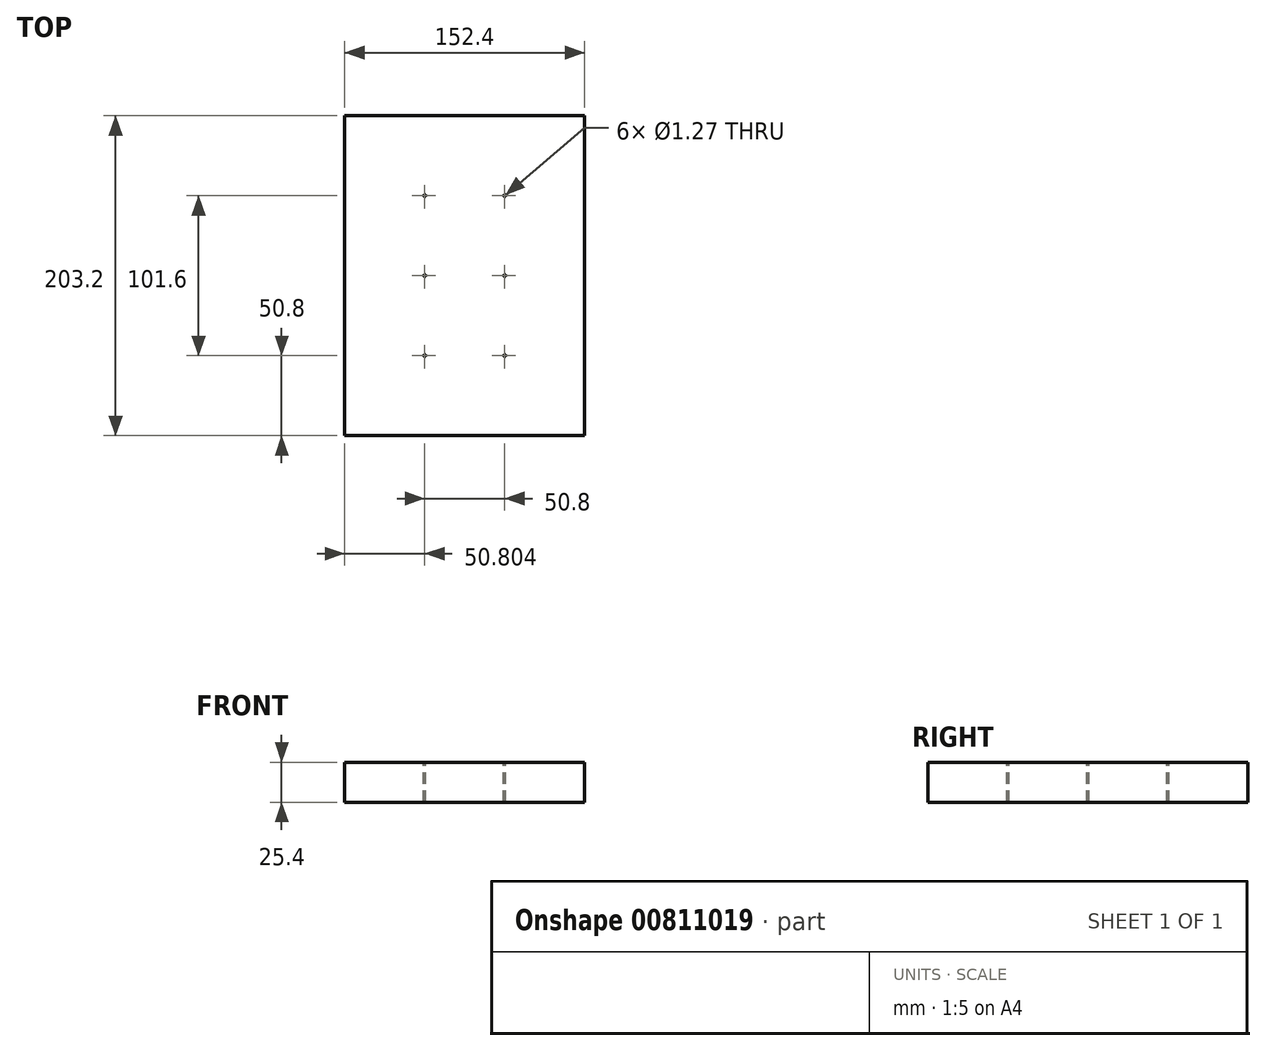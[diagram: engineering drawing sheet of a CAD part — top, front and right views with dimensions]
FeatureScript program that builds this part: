
annotation { "Feature Type Name" : "Feature", "Feature Type Description" : "" }
export const myFeature = defineFeature(function(context is Context, id is Id, definition is map)
    precondition{}
    {
        {
            var Q0;
            Q0=qCreatedBy(makeId("Top.planeOp"),FACE);
            var sketch = newSketch(context, id + "F0", { "sketchPlane" : qUnion([Q0])});
            skLineSegment(sketch, "E0", {"start": v(-77.99, 0) * mm, "end": v(74.41, 0) * mm});
            skLineSegment(sketch, "E1", {"start": v(74.41, 0) * mm, "end": v(74.41, 203.2) * mm});
            skLineSegment(sketch, "E2", {"start": v(74.41, 203.2) * mm, "end": v(-77.99, 203.2) * mm});
            skLineSegment(sketch, "E3", {"start": v(-77.99, 203.2) * mm, "end": v(-77.99, 0) * mm});
            skSolve(sketch);
        }
        {
            var Q0;
            Q0=makeQuery(id+"F0.imprint","IMPRINT",FACE,{"disambiguationData":[TD([[makeQuery(id+"F0.imprint","IMPRINT",EDGE,{"derivedFrom":sQuery(id+"F0.wireOp",EDGE,"E0")}),1.0]])]});
            extrude(context, id + "F1", {"entities" : qUnion([Q0]), "depth" : 25.4 * mm, "offsetDistance" : 25.4 * mm});
        }
        {
            var Q0;
            Q0=makeQuery(id+"F1.opExtrude","CAP_FACE",FACE,{"disambiguationData":[OSD([sQuery(id+"F0.wireOp",EDGE,"E0"),sQuery(id+"F0.wireOp",EDGE,"E1"),sQuery(id+"F0.wireOp",EDGE,"E2"),sQuery(id+"F0.wireOp",EDGE,"E3")])],"isStart":false});
            var sketch = newSketch(context, id + "F2", { "sketchPlane" : qUnion([Q0])});
            skCircle(sketch, "E4", {"center": v(23.61, 152.4) * mm, "radius": 0.64 * mm});
            skCircle(sketch, "E5", {"center": v(23.61, 101.6) * mm, "radius": 0.64 * mm});
            skCircle(sketch, "E6", {"center": v(23.61, 50.8) * mm, "radius": 0.64 * mm});
            skCircle(sketch, "E7", {"center": v(-27.19, 152.4) * mm, "radius": 0.64 * mm});
            skCircle(sketch, "E8", {"center": v(-27.19, 101.6) * mm, "radius": 0.64 * mm});
            skCircle(sketch, "E9", {"center": v(-27.19, 50.8) * mm, "radius": 0.64 * mm});
            skSolve(sketch);
        }
        {
            var Q0;
            Q0 = qSketchRegion(id + "F2", true);
            extrude(context, id + "F3", {"entities" : qUnion([Q0]), "operationType" : NewBodyOperationType.REMOVE, "oppositeDirection" : true, "depth" : 25.4 * mm, "offsetDistance" : 25.4 * mm});
        }
    });
